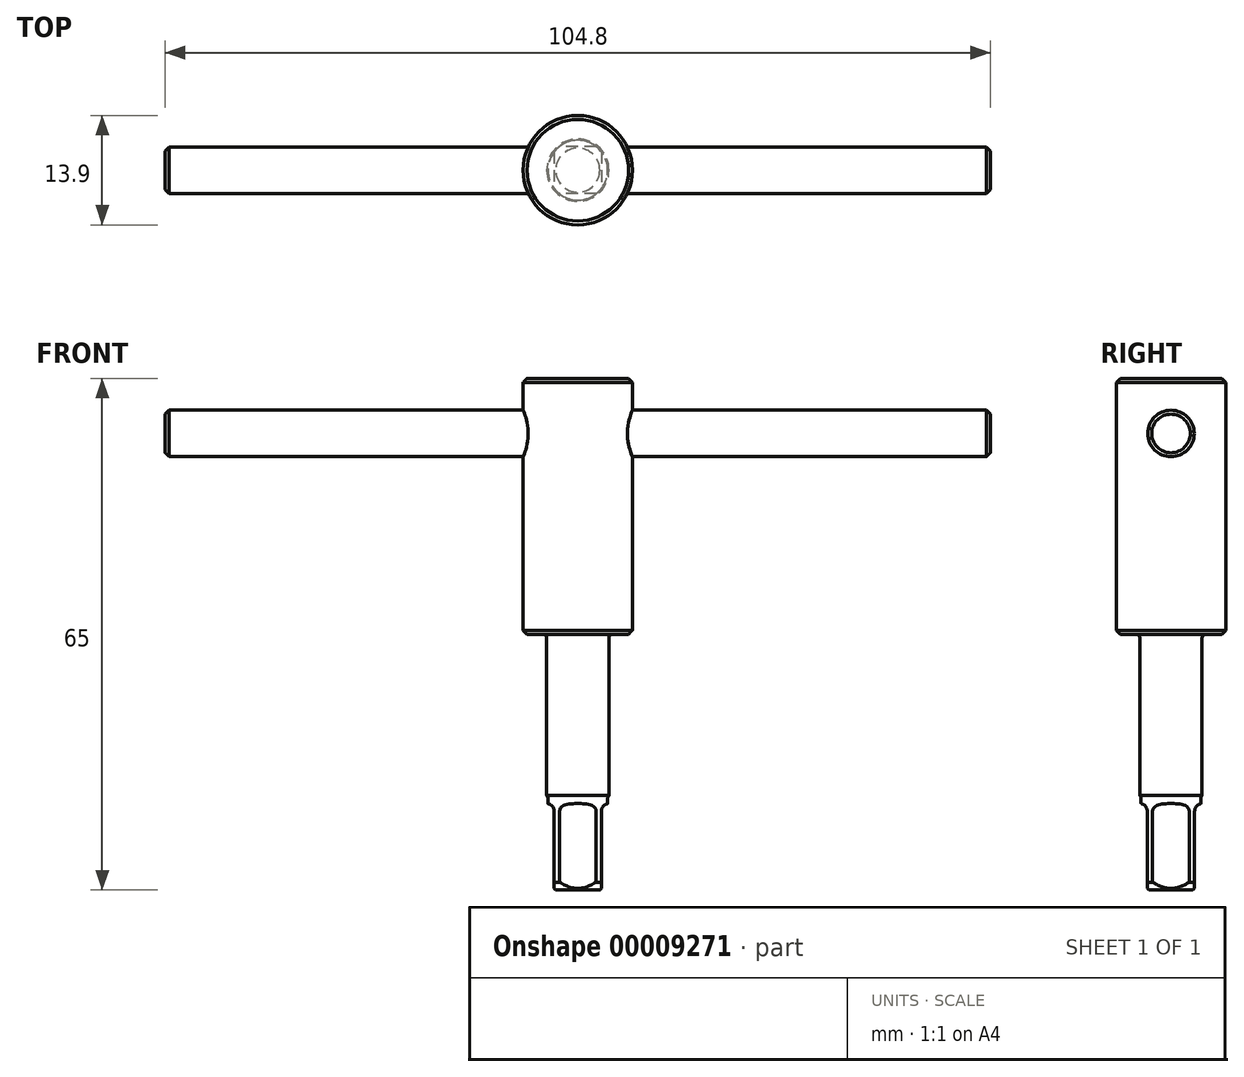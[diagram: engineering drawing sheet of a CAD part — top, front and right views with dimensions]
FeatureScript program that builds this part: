
annotation { "Feature Type Name" : "Feature", "Feature Type Description" : "" }
export const myFeature = defineFeature(function(context is Context, id is Id, definition is map)
    precondition{}
    {
        {
            var Q0;
            Q0=qCreatedBy(makeId("Front.planeOp"),FACE);
            var sketch = newSketch(context, id + "F0", { "sketchPlane" : qUnion([Q0])});
            skLineSegment(sketch, "E0", {"start": v(0, 0) * mm, "end": v(0, 65) * mm, "construction": true});
            skLineSegment(sketch, "E1", {"start": v(0, 65) * mm, "end": v(6.95, 65) * mm});
            skLineSegment(sketch, "E2", {"start": v(6.95, 65) * mm, "end": v(6.95, 32.5) * mm});
            skLineSegment(sketch, "E3", {"start": v(6.95, 32.5) * mm, "end": v(3.95, 32.5) * mm});
            skLineSegment(sketch, "E4", {"start": v(3.95, 32.5) * mm, "end": v(3.95, 12) * mm});
            skLineSegment(sketch, "E5", {"start": v(3.8, 0) * mm, "end": v(0, 0) * mm});
            skLineSegment(sketch, "E6", {"start": v(0, 0) * mm, "end": v(0, 65) * mm});
            skLineSegment(sketch, "E7", {"start": v(3.8, 0) * mm, "end": v(3.8, 12) * mm});
            skLineSegment(sketch, "E8", {"start": v(3.8, 12) * mm, "end": v(3.95, 12) * mm});
            skSolve(sketch);
        }
        {
            var Q0;
            Q0 = qSketchRegion(id + "F0", true);
            var Q1;
            Q1=sQuery(id+"F0.wireOp",EDGE,"E0");
            revolve(context, id + "F1", {"entities" : qUnion([Q0]), "axis" : qUnion([Q1]), "revolveType" : RevolveType.FULL});
        }
        {
            var Q0;
            Q0=makeQuery(id+"F1.opRevolve","SWEPT_EDGE",EDGE,{"disambiguationData":[OSD([sQuery(id+"F0.wireOp",EDGE,"E5"),sQuery(id+"F0.wireOp",EDGE,"E7")])]});
            chamfer(context, id + "F2", {"entities" : qUnion([Q0]), "width" : 1 * mm, "tangentPropagation" : true});
        }
        {
            var Q0;
            Q0=qCreatedBy(makeId("Right.planeOp"),FACE);
            var sketch = newSketch(context, id + "F3", { "sketchPlane" : qUnion([Q0])});
            skCircle(sketch, "E9", {"center": v(0, 58) * mm, "radius": 2.95 * mm});
            skSolve(sketch);
        }
        {
            var Q0;
            Q0 = qSketchRegion(id + "F3", true);
            extrude(context, id + "F4", {"entities" : qUnion([Q0]), "operationType" : NewBodyOperationType.ADD, "depth" : 104.8 * mm, "symmetric" : true});
        }
        {
            var Q0;
            Q0=makeQuery(id+"F1.opRevolve","SWEPT_EDGE",EDGE,{"disambiguationData":[OSD([sQuery(id+"F0.wireOp",EDGE,"E1"),sQuery(id+"F0.wireOp",EDGE,"E2")])]});
            var Q1;
            Q1=makeQuery(id+"F1.opRevolve","SWEPT_EDGE",EDGE,{"disambiguationData":[OSD([sQuery(id+"F0.wireOp",EDGE,"E2"),sQuery(id+"F0.wireOp",EDGE,"E3")])]});
            var Q2;
            Q2=makeQuery(id+"F4.opExtrude","CAP_EDGE",EDGE,{"disambiguationData":[OSD([sQuery(id+"F3.wireOp",EDGE,"E9")])],"isStart":false});
            var Q3;
            Q3=makeQuery(id+"F4.opExtrude","CAP_EDGE",EDGE,{"disambiguationData":[OSD([sQuery(id+"F3.wireOp",EDGE,"E9")])],"isStart":true});
            chamfer(context, id + "F5", {"entities" : qUnion([Q0, Q1, Q2, Q3]), "width" : .5 * mm, "tangentPropagation" : true});
        }
        {
            var Q0;
            Q0=makeQuery(id+"F1.opRevolve","SWEPT_EDGE",EDGE,{"disambiguationData":[OSD([sQuery(id+"F0.wireOp",EDGE,"E3"),sQuery(id+"F0.wireOp",EDGE,"E4")])]});
            var Q1;
            Q1=makeQuery(id+"F1.opRevolve","SWEPT_EDGE",EDGE,{"disambiguationData":[OSD([sQuery(id+"F0.wireOp",EDGE,"E7"),sQuery(id+"F0.wireOp",EDGE,"E8")])]});
            fillet(context, id + "F6", {"entities" : qUnion([Q0, Q1]), "radius" : .5 * mm, "tangentPropagation" : true, "allowEdgeOverflow" : false});
        }
        {
            var Q0;
            Q0=makeQuery(id+"F1.opRevolve","SWEPT_FACE",FACE,{"disambiguationData":[OSD([sQuery(id+"F0.wireOp",EDGE,"E5")])]});
            var sketch = newSketch(context, id + "F7", { "sketchPlane" : qUnion([Q0])});
            skLineSegment(sketch, "E10.bottom", {"start": v(3, -3) * mm, "end": v(-3, -3) * mm});
            skLineSegment(sketch, "E10.top", {"start": v(3, 3) * mm, "end": v(-3, 3) * mm});
            skLineSegment(sketch, "E10.left", {"start": v(3, -3) * mm, "end": v(3, 3) * mm});
            skLineSegment(sketch, "E10.right", {"start": v(-3, -3) * mm, "end": v(-3, 3) * mm});
            skPoint(sketch, "E10.middle", {"position": v(0, 0) * mm});
            skCircle(sketch, "E11", {"center": v(0, 0) * mm, "radius": 25 * mm});
            skSolve(sketch);
        }
        {
            var Q0;
            Q0 = qSketchRegion(id + "F7", true);
            extrude(context, id + "F8", {"entities" : qUnion([Q0]), "operationType" : NewBodyOperationType.REMOVE, "oppositeDirection" : true, "depth" : 11 * mm});
        }
        {
            var Q0;
            Q0=makeQuery(id+"F8.boolean.opBoolean","COPY",EDGE,{"derivedFrom":makeQuery(id+"F8.opExtrude","CAP_EDGE",EDGE,{"disambiguationData":[OSD([sQuery(id+"F7.wireOp",EDGE,"E10.top")])],"isStart":false})});
            var Q1;
            Q1=makeQuery(id+"F8.boolean.opBoolean","COPY",EDGE,{"derivedFrom":makeQuery(id+"F8.opExtrude","CAP_EDGE",EDGE,{"disambiguationData":[OSD([sQuery(id+"F7.wireOp",EDGE,"E10.right")])],"isStart":false})});
            var Q2;
            Q2=makeQuery(id+"F8.boolean.opBoolean","COPY",EDGE,{"derivedFrom":makeQuery(id+"F8.opExtrude","CAP_EDGE",EDGE,{"disambiguationData":[OSD([sQuery(id+"F7.wireOp",EDGE,"E10.bottom")])],"isStart":false})});
            var Q3;
            Q3=makeQuery(id+"F8.boolean.opBoolean","COPY",EDGE,{"derivedFrom":makeQuery(id+"F8.opExtrude","CAP_EDGE",EDGE,{"disambiguationData":[OSD([sQuery(id+"F7.wireOp",EDGE,"E10.left")])],"isStart":false})});
            fillet(context, id + "F9", {"entities" : qUnion([Q0, Q1, Q2, Q3]), "radius" : 1 * mm, "tangentPropagation" : true, "allowEdgeOverflow" : false});
        }
    });
